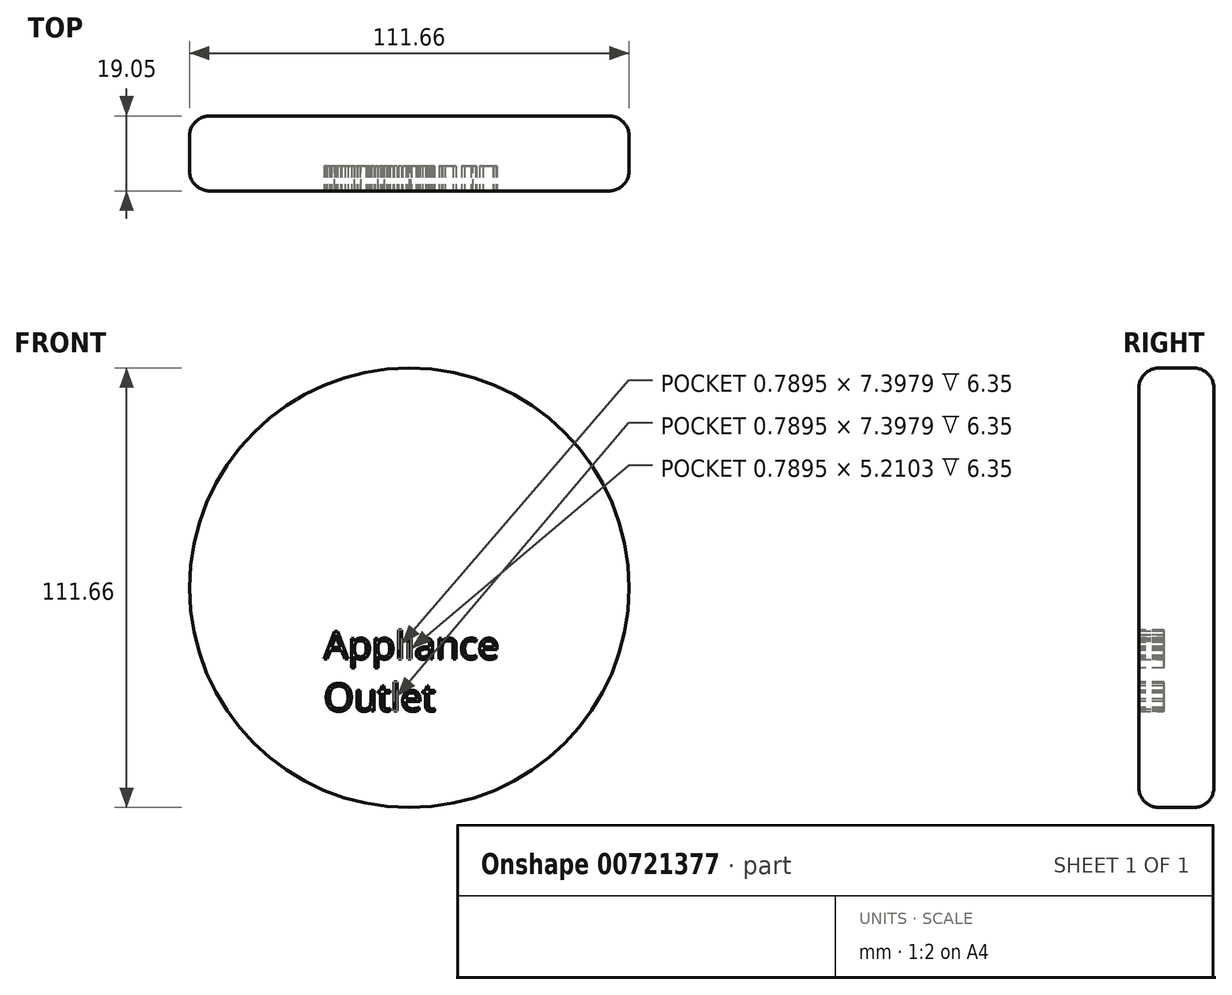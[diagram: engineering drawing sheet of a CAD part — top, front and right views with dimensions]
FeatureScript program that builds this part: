
annotation { "Feature Type Name" : "Feature", "Feature Type Description" : "" }
export const myFeature = defineFeature(function(context is Context, id is Id, definition is map)
    precondition{}
    {
        {
            var Q0;
            Q0=qCreatedBy(makeId("Front.planeOp"),FACE);
            var sketch = newSketch(context, id + "F0", { "sketchPlane" : qUnion([Q0])});
            skCircle(sketch, "E0", {"center": v(0, 0) * mm, "radius": 55.83 * mm});
            skSolve(sketch);
        }
        {
            var Q0;
            Q0=makeQuery(id+"F0.imprint","IMPRINT",FACE,{"disambiguationData":[TD([[makeQuery(id+"F0.imprint","IMPRINT",EDGE,{"derivedFrom":sQuery(id+"F0.wireOp",EDGE,"E0")}),1.0]])]});
            extrude(context, id + "F1", {"entities" : qUnion([Q0]), "depth" : 19.05 * mm, "offsetDistance" : 25.4 * mm});
        }
        {
            var Q0;
            Q0=makeQuery(id+"F1.opExtrude","CAP_FACE",FACE,{"disambiguationData":[OSD([sQuery(id+"F0.wireOp",EDGE,"E0")])],"isStart":false});
            fillet(context, id + "F2", {"entities" : qUnion([Q0]), "radius" : 5.08 * mm, "tangentPropagation" : true, "allowEdgeOverflow" : false});
        }
        {
            var Q0;
            Q0=makeQuery(id+"F1.opExtrude","CAP_FACE",FACE,{"disambiguationData":[OSD([sQuery(id+"F0.wireOp",EDGE,"E0")])],"isStart":true});
            fillet(context, id + "F3", {"entities" : qUnion([Q0]), "radius" : 5.08 * mm, "tangentPropagation" : true, "allowEdgeOverflow" : false});
        }
        {
            var Q0;
            Q0=makeQuery(id+"F1.opExtrude","CAP_FACE",FACE,{"disambiguationData":[OSD([sQuery(id+"F0.wireOp",EDGE,"E0")])],"isStart":false});
            var sketch = newSketch(context, id + "F4", { "sketchPlane" : qUnion([Q0])});
            skText(sketch, "E1", { "text": "Appliance\nOutlet", "fontName": "OpenSans-Regular.ttf"});
            const initialGuessF4  = {"E1": [-0.0217, -0.01808, 1, 0, 0.00701]};
            skSetInitialGuess(sketch, initialGuessF4);
            skSolve(sketch);
        }
        {
            var Q0;
            Q0 = qSketchRegion(id + "F4", true);
            extrude(context, id + "F5", {"entities" : qUnion([Q0]), "operationType" : NewBodyOperationType.REMOVE, "oppositeDirection" : true, "depth" : 6.35 * mm, "offsetDistance" : 25.4 * mm});
        }
    });
